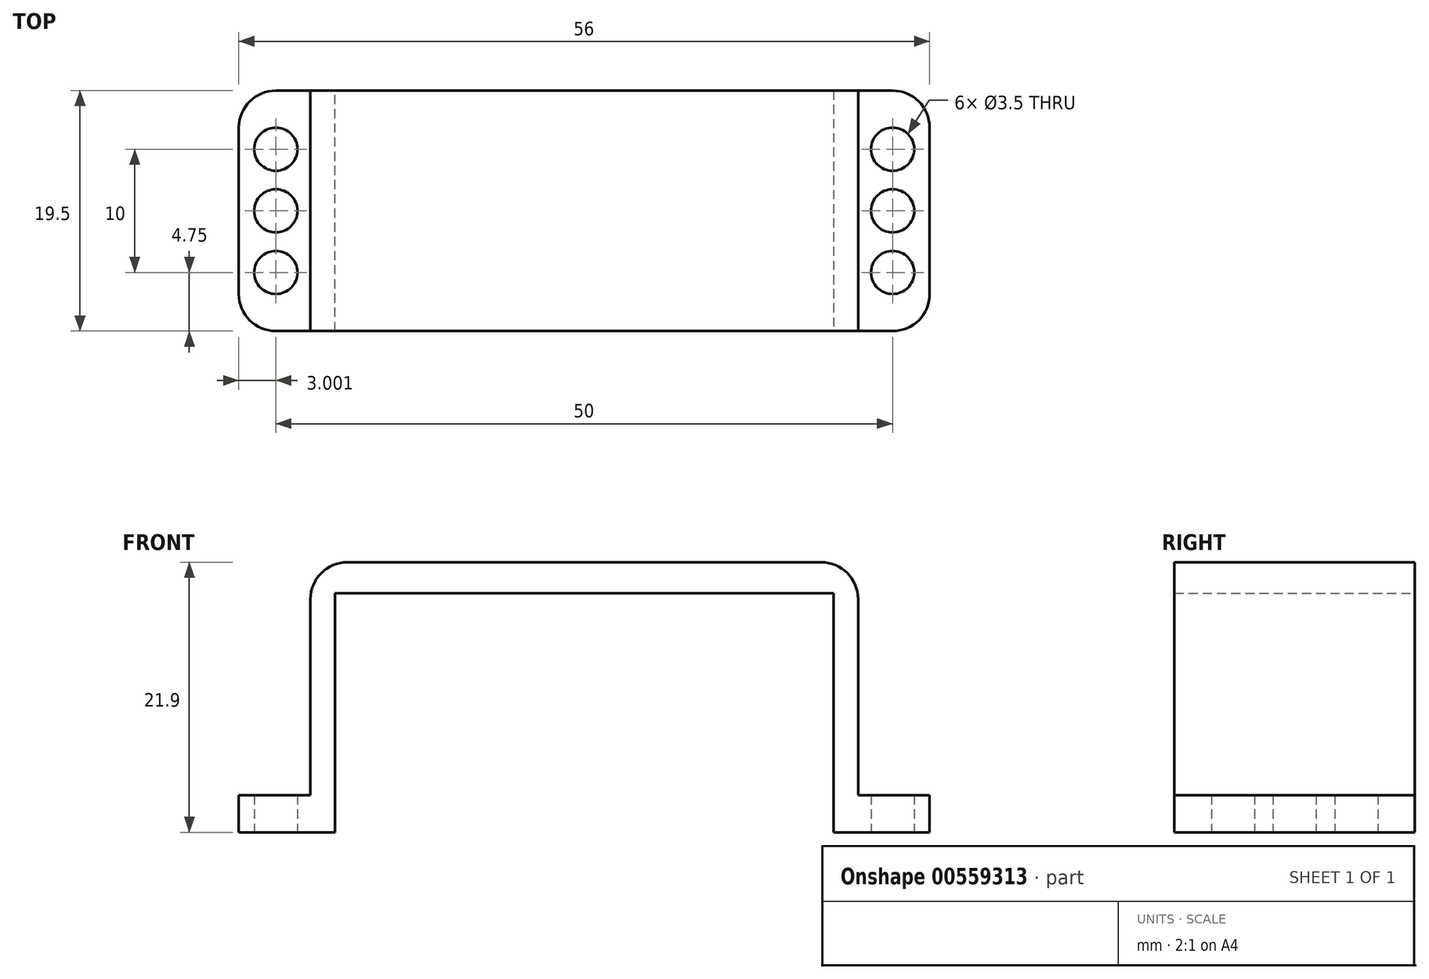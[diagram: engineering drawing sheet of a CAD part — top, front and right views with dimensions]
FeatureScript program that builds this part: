
annotation { "Feature Type Name" : "Feature", "Feature Type Description" : "" }
export const myFeature = defineFeature(function(context is Context, id is Id, definition is map)
    precondition{}
    {
        {
            var Q0;
            Q0=qCreatedBy(makeId("Top.planeOp"),FACE);
            var sketch = newSketch(context, id + "F0", { "sketchPlane" : qUnion([Q0])});
            skLineSegment(sketch, "E0.bottom", {"start": v(-24.16, 19.5) * mm, "end": v(16.24, 19.5) * mm, "construction": true});
            skLineSegment(sketch, "E0.top", {"start": v(-24.16, 0) * mm, "end": v(16.24, 0) * mm, "construction": true});
            skLineSegment(sketch, "E0.left", {"start": v(-24.16, 19.5) * mm, "end": v(-24.16, 0) * mm});
            skLineSegment(sketch, "E0.right", {"start": v(16.24, 19.5) * mm, "end": v(16.24, 0) * mm});
            skLineSegment(sketch, "E1", {"start": v(16.24, 19.5) * mm, "end": v(21.04, 19.5) * mm});
            skLineSegment(sketch, "E2", {"start": v(21.04, 0) * mm, "end": v(16.24, 0) * mm});
            skLineSegment(sketch, "E3", {"start": v(-24.16, 19.5) * mm, "end": v(-28.96, 19.5) * mm});
            skLineSegment(sketch, "E4", {"start": v(-28.96, 0) * mm, "end": v(-24.16, 0) * mm});
            skLineSegment(sketch, "E5", {"start": v(-28.96, 9.75) * mm, "end": v(-28.96, 4.75) * mm, "construction": true});
            skLineSegment(sketch, "E6", {"start": v(-28.96, 4.75) * mm, "end": v(-28.96, 0) * mm, "construction": true});
            skLineSegment(sketch, "E7", {"start": v(-28.96, 9.75) * mm, "end": v(-28.96, 14.75) * mm, "construction": true});
            skLineSegment(sketch, "E8", {"start": v(-28.96, 14.75) * mm, "end": v(-28.96, 19.5) * mm, "construction": true});
            skLineSegment(sketch, "E9", {"start": v(21.04, 9.75) * mm, "end": v(21.04, 14.75) * mm, "construction": true});
            skLineSegment(sketch, "E10", {"start": v(21.04, 14.75) * mm, "end": v(21.04, 19.5) * mm, "construction": true});
            skLineSegment(sketch, "E11", {"start": v(21.04, 9.75) * mm, "end": v(21.04, 4.75) * mm, "construction": true});
            skLineSegment(sketch, "E12", {"start": v(21.04, 4.75) * mm, "end": v(21.04, 0) * mm, "construction": true});
            skCircle(sketch, "E13", {"center": v(-28.96, 14.75) * mm, "radius": 1.75 * mm});
            skCircle(sketch, "E14", {"center": v(-28.96, 4.75) * mm, "radius": 1.75 * mm});
            skCircle(sketch, "E15", {"center": v(21.04, 14.75) * mm, "radius": 1.75 * mm});
            skCircle(sketch, "E16", {"center": v(21.04, 9.75) * mm, "radius": 1.75 * mm});
            skCircle(sketch, "E17", {"center": v(21.04, 4.75) * mm, "radius": 1.75 * mm});
            skCircle(sketch, "E18", {"center": v(-28.96, 9.75) * mm, "radius": 1.75 * mm});
            skLineSegment(sketch, "E19", {"start": v(21.04, 19.5) * mm, "end": v(24.04, 19.5) * mm});
            skLineSegment(sketch, "E20", {"start": v(24.04, 19.5) * mm, "end": v(24.04, 0) * mm});
            skLineSegment(sketch, "E21", {"start": v(24.04, 0) * mm, "end": v(21.04, 0) * mm});
            skLineSegment(sketch, "E22", {"start": v(-28.96, 19.5) * mm, "end": v(-31.96, 19.5) * mm});
            skLineSegment(sketch, "E23", {"start": v(-31.96, 19.5) * mm, "end": v(-31.96, 0) * mm});
            skLineSegment(sketch, "E24", {"start": v(-31.96, 0) * mm, "end": v(-28.96, 0) * mm});
            skLineSegment(sketch, "E25", {"start": v(-24.16, 9.75) * mm, "end": v(-26.16, 9.75) * mm, "construction": true});
            skLineSegment(sketch, "E26", {"start": v(16.24, 9.75) * mm, "end": v(18.24, 9.75) * mm, "construction": true});
            skLineSegment(sketch, "E27", {"start": v(-26.16, 9.75) * mm, "end": v(-26.16, 19.5) * mm});
            skLineSegment(sketch, "E28", {"start": v(-26.16, 9.75) * mm, "end": v(-26.16, 0) * mm});
            skLineSegment(sketch, "E29", {"start": v(18.24, 19.5) * mm, "end": v(18.24, 0) * mm});
            skSolve(sketch);
        }
        {
            var Q0;
            {var subQ1=sQuery(id+"F0.wireOp",EDGE,"E0.left");Q0=makeQuery(id+"F0.imprint","IMPRINT",FACE,{"disambiguationData":[TD([[makeQuery(id+"F0.imprint","IMPRINT",EDGE,{"derivedFrom":subQ1}),-1.0]])]});}
            var Q1;
            {var subQ0=sQuery(id+"F0.wireOp",EDGE,"E0.right");Q1=makeQuery(id+"F0.imprint","IMPRINT",FACE,{"disambiguationData":[TD([[makeQuery(id+"F0.imprint","IMPRINT",EDGE,{"derivedFrom":subQ0}),1.0]])]});}
            var Q2;
            Q2=sQuery(id+"F0.wireOp",EDGE,"E27");
            extrude(context, id + "F1", {"entities" : qUnion([Q0, Q1]), "surfaceEntities" : qUnion([Q2]), "depth" : 21.9 * mm, "offsetDistance" : 25 * mm});
        }
        {
            var Q0;
            Q0=makeQuery(id+"F1.opExtrude","SWEPT_FACE",FACE,{"disambiguationData":[OSD([sQuery(id+"F0.wireOp",EDGE,"E0.right")])]});
            var sketch = newSketch(context, id + "F2", { "sketchPlane" : qUnion([Q0])});
            skLineSegment(sketch, "E30", {"start": v(-19.5, 21.9) * mm, "end": v(-19.5, 19.4) * mm});
            skLineSegment(sketch, "E31", {"start": v(-19.5, 19.4) * mm, "end": v(0, 19.4) * mm});
            skLineSegment(sketch, "E32", {"start": v(0, 19.4) * mm, "end": v(0, 21.9) * mm});
            skLineSegment(sketch, "E33", {"start": v(0, 21.9) * mm, "end": v(-19.5, 21.9) * mm});
            skSolve(sketch);
        }
        {
            var Q0;
            Q0=makeQuery(id+"F2.imprint","IMPRINT",FACE,{"disambiguationData":[TD([[makeQuery(id+"F2.imprint","IMPRINT",EDGE,{"derivedFrom":sQuery(id+"F2.wireOp",EDGE,"E30")}),1.0]])]});
            extrude(context, id + "F3", {"entities" : qUnion([Q0]), "operationType" : NewBodyOperationType.ADD, "endBound" : BoundingType.UP_TO_NEXT, "depth" : 41.1 * mm, "offsetDistance" : 25 * mm});
        }
        {
            var Q0;
            Q0=makeQuery(id+"F0.imprint","IMPRINT",FACE,{"disambiguationData":[TD([[makeQuery(id+"F0.imprint","IMPRINT",EDGE,{"derivedFrom":sQuery(id+"F0.wireOp",EDGE,"E13")}),-1.0]])]});
            var Q1;
            Q1=makeQuery(id+"F0.imprint","IMPRINT",FACE,{"disambiguationData":[TD([[makeQuery(id+"F0.imprint","IMPRINT",EDGE,{"derivedFrom":sQuery(id+"F0.wireOp",EDGE,"E15")}),-1.0]])]});
            extrude(context, id + "F4", {"entities" : qUnion([Q0, Q1]), "operationType" : NewBodyOperationType.ADD, "depth" : 3 * mm, "offsetDistance" : 25 * mm});
        }
        {
            var Q0;
            Q0=makeQuery(id+"F1.opExtrude","CAP_EDGE",EDGE,{"disambiguationData":[OSD([sQuery(id+"F0.wireOp",EDGE,"E29")])],"isStart":false});
            var Q1;
            Q1=makeQuery(id+"F1.opExtrude","CAP_EDGE",EDGE,{"disambiguationData":[OSD([sQuery(id+"F0.wireOp",EDGE,"E27"),sQuery(id+"F0.wireOp",EDGE,"E28")])],"isStart":false});
            var Q2;
            Q2=makeQuery(id+"F4.opExtrude","SWEPT_EDGE",EDGE,{"disambiguationData":[OSD([sQuery(id+"F0.wireOp",EDGE,"E20"),sQuery(id+"F0.wireOp",EDGE,"E21")])]});
            var Q3;
            Q3=makeQuery(id+"F4.opExtrude","SWEPT_EDGE",EDGE,{"disambiguationData":[OSD([sQuery(id+"F0.wireOp",EDGE,"E19"),sQuery(id+"F0.wireOp",EDGE,"E20")])]});
            var Q4;
            Q4=makeQuery(id+"F4.opExtrude","SWEPT_EDGE",EDGE,{"disambiguationData":[OSD([sQuery(id+"F0.wireOp",EDGE,"E22"),sQuery(id+"F0.wireOp",EDGE,"E23")])]});
            var Q5;
            Q5=makeQuery(id+"F4.opExtrude","SWEPT_EDGE",EDGE,{"disambiguationData":[OSD([sQuery(id+"F0.wireOp",EDGE,"E23"),sQuery(id+"F0.wireOp",EDGE,"E24")])]});
            fillet(context, id + "F5", {"entities" : qUnion([Q0, Q1, Q2, Q3, Q4, Q5]), "radius" : 3 * mm, "tangentPropagation" : true, "allowEdgeOverflow" : false});
        }
    });
